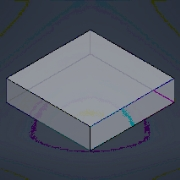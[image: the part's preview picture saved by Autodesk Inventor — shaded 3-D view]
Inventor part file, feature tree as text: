
AUTODESK INVENTOR PART (.ipt)
format: ipt  version: 2024.3 (Build 283343000, 343)  size: 135,168 bytes
history: native  units: mm
features: extrude x1, sketch x1
ambient origin geometry x8: Origin, YZ Plane, XZ Plane, XY Plane, X Axis, Y Axis, Z Axis, Center Point
bodies: Solid1 (feature_tree)
feature tree (2):
  extrude  "Extrusion1"  Depth=150.0mm
  sketch  "Sketch1"  dims[d0=150.0mm d1=150.0mm d2=60.0mm d3=0.0mm]
